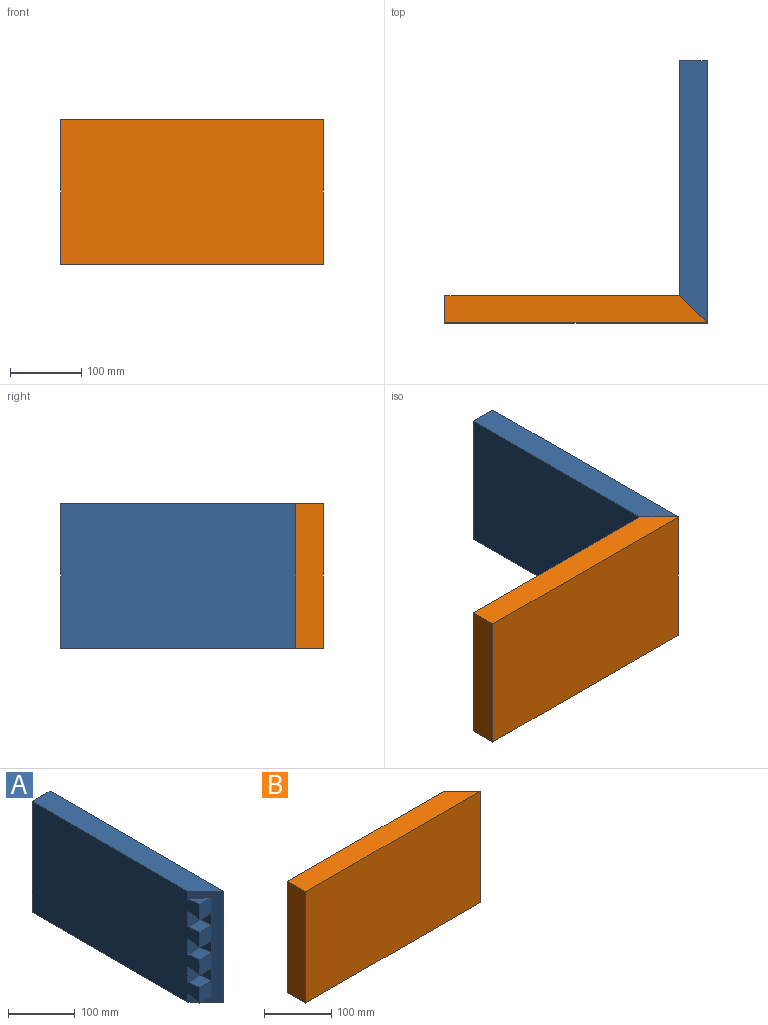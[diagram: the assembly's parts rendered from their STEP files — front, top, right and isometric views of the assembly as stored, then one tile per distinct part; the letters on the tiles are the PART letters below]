
ASSEMBLY  parts=2 mates=1
PART A: 24 faces, bbox 38.1x368.3x203.2 mm
  f0: plane 25.4x25.4mm, normal (0,0.12,-0.99), area 325.1mm2, adj f15,f18,f22
  f1: plane 368.3x38.1mm, normal (0,0,1), area 13306.4mm2, adj f17,f18,f22,f23
  f2: plane 25.4x25.4mm, normal (0,0.12,0.99), area 325.1mm2, adj f3,f18,f22
  f3: plane 28.58x25.4mm, normal (0,-1,0), area 725.8mm2, adj f2,f4,f18,f22
  f4: plane 25.4x25.4mm, normal (0,0.12,-0.99), area 650.2mm2, adj f3,f5,f18,f19
  f5: plane 28.58x25.4mm, normal (0,-1,0), area 725.8mm2, adj f4,f6,f18,f19
  f6: plane 25.4x25.4mm, normal (0,0.12,0.99), area 650.2mm2, adj f5,f7,f18,f19
  f7: plane 28.58x25.4mm, normal (0,-1,0), area 725.8mm2, adj f6,f8,f18,f22
  f8: plane 25.4x25.4mm, normal (0,0.12,-0.99), area 650.2mm2, adj f7,f9,f18,f20
  f9: plane 28.58x25.4mm, normal (0,-1,0), area 725.8mm2, adj f8,f10,f18,f20
  f10: plane 25.4x25.4mm, normal (0,0.12,0.99), area 650.2mm2, adj f9,f11,f18,f20
  f11: plane 28.58x25.4mm, normal (0,-1,0), area 725.8mm2, adj f10,f12,f18,f22
  f12: plane 25.4x25.4mm, normal (0,0.12,-0.99), area 650.2mm2, adj f11,f13,f18,f21
  f13: plane 28.58x25.4mm, normal (0,-1,0), area 725.8mm2, adj f12,f14,f18,f21
  f14: plane 25.4x25.4mm, normal (0,0.12,0.99), area 650.2mm2, adj f13,f15,f18,f21
  f15: plane 28.58x25.4mm, normal (0,-1,0), area 725.8mm2, adj f0,f14,f18,f22
  f16: plane 368.3x38.1mm, normal (0,0,-1), area 13306.4mm2, adj f17,f18,f22,f23
  f17: plane 203.2x38.1mm, normal (0,1,0), area 7741.9mm2, adj f1,f16,f18,f23
  f18: plane 355.6x203.2mm, normal (-1,0,0), area 69677.3mm2, adj f0,f1,f2,f3,f4,f5,f6,f7
  f19: plane 28.58x25.4mm, normal (-1,0,0), area 645.2mm2, adj f4,f5,f6,f22
  f20: plane 28.58x25.4mm, normal (-1,0,0), area 645.2mm2, adj f8,f9,f10,f22
  f21: plane 28.58x25.4mm, normal (-1,0,0), area 645.2mm2, adj f12,f13,f14,f22
  f22: plane 203.2x38.1mm, normal (-0.71,-0.71,0), area 4562mm2, adj f0,f1,f2,f3,f7,f11,f15,f16
  f23: plane 368.3x203.2mm, normal (1,0,0), area 74838.6mm2, adj f1,f16,f17,f22
PART B: 25 faces, bbox 368.3x38.1x203.2 mm
  f0: plane 355.6x203.2mm, normal (0,1,0), area 69274.1mm2, adj f2,f4,f5,f6,f7,f8,f9,f10
  f1: plane 25.4x25.4mm, normal (0,-0.12,-0.99), area 325.1mm2, adj f18,f22,f24
  f2: plane 368.3x38.1mm, normal (0,0,-1), area 13306.4mm2, adj f0,f8,f23,f24
  f3: plane 25.4x25.4mm, normal (0,-0.12,0.99), area 325.1mm2, adj f13,f19,f24
  f4: plane 28.58x25.4mm, normal (1,0,0), area 645.2mm2, adj f0,f14,f17,f24
  f5: plane 28.58x25.4mm, normal (1,0,0), area 645.2mm2, adj f0,f10,f12,f24
  f6: plane 28.58x25.4mm, normal (1,0,0), area 645.2mm2, adj f0,f9,f15,f24
  f7: plane 368.3x38.1mm, normal (0,0,1), area 13306.4mm2, adj f0,f8,f23,f24
  f8: plane 203.2x38.1mm, normal (-1,0,0), area 7741.9mm2, adj f0,f2,f7,f23
  f9: plane 25.4x25.4mm, normal (0,-0.12,-0.99), area 650.2mm2, adj f0,f6,f11,f20
  f10: plane 25.4x25.4mm, normal (0,-0.12,0.99), area 650.2mm2, adj f0,f5,f11,f20
  f11: plane 28.58x25.4mm, normal (1,0,0), area 645.2mm2, adj f0,f9,f10,f20
  f12: plane 25.4x25.4mm, normal (0,-0.12,-0.99), area 650.2mm2, adj f0,f5,f13,f19
  f13: plane 28.58x25.4mm, normal (1,0,0), area 645.2mm2, adj f0,f3,f12,f19
  f14: plane 25.4x25.4mm, normal (0,-0.12,-0.99), area 650.2mm2, adj f0,f4,f16,f21
  f15: plane 25.4x25.4mm, normal (0,-0.12,0.99), area 650.2mm2, adj f0,f6,f16,f21
  f16: plane 28.58x25.4mm, normal (1,0,0), area 645.2mm2, adj f0,f14,f15,f21
  f17: plane 25.4x25.4mm, normal (0,-0.12,0.99), area 650.2mm2, adj f0,f4,f18,f22
  f18: plane 28.58x25.4mm, normal (1,0,0), area 645.2mm2, adj f0,f1,f17,f22
  f19: plane 28.58x25.4mm, normal (0,1,0), area 725.8mm2, adj f3,f12,f13,f24
  f20: plane 28.58x25.4mm, normal (0,1,0), area 725.8mm2, adj f9,f10,f11,f24
  f21: plane 28.58x25.4mm, normal (0,1,0), area 725.8mm2, adj f14,f15,f16,f24
  f22: plane 28.58x25.4mm, normal (0,1,0), area 725.8mm2, adj f1,f17,f18,f24
  f23: plane 368.3x203.2mm, normal (0,-1,0), area 74838.6mm2, adj f2,f7,f8,f24
  f24: plane 203.2x38.1mm, normal (0.71,0.71,0), area 4562mm2, adj f0,f1,f2,f3,f4,f5,f6,f7
PLACE A at identity
PLACE B t=(25.4,0,0)mm
MATE fastened B.f17 <-> A.f4  axis (0,-0.12,0.99) through (12.7,-12.7,63.5)mm
